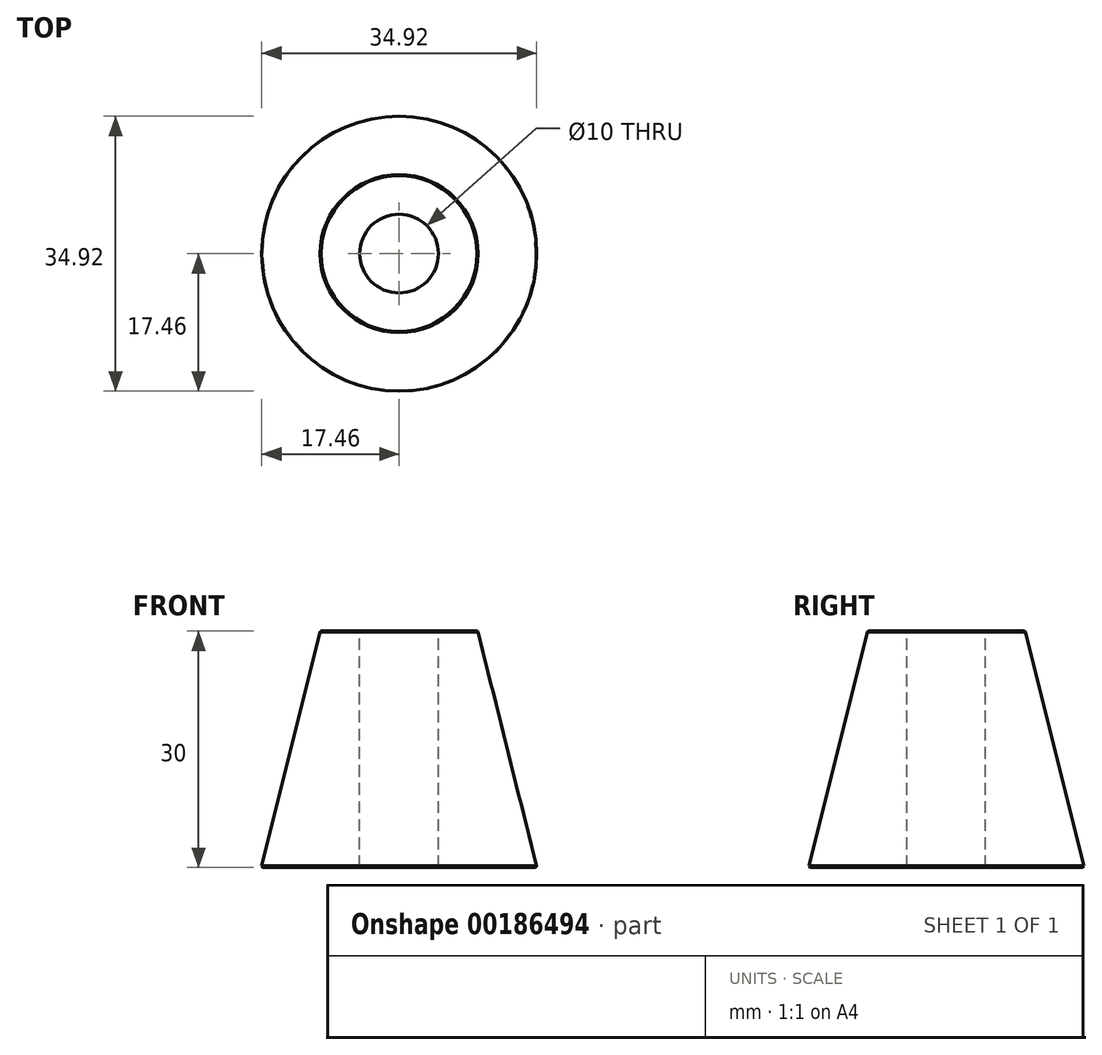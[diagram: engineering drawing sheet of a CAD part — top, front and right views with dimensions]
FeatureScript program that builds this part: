
annotation { "Feature Type Name" : "Feature", "Feature Type Description" : "" }
export const myFeature = defineFeature(function(context is Context, id is Id, definition is map)
    precondition{}
    {
        {
            var Q0;
            Q0=qCreatedBy(makeId("Front.planeOp"),FACE);
            var sketch = newSketch(context, id + "F0", { "sketchPlane" : qUnion([Q0])});
            skLineSegment(sketch, "E0", {"start": v(0, 0) * mm, "end": v(-17.5, 0) * mm});
            skLineSegment(sketch, "E1", {"start": v(-17.5, 0) * mm, "end": v(-10, 30) * mm});
            skLineSegment(sketch, "E2", {"start": v(-10, 30) * mm, "end": v(0, 30) * mm});
            skLineSegment(sketch, "E3", {"start": v(0, 30) * mm, "end": v(0, 0) * mm});
            skLineSegment(sketch, "E4", {"start": v(0, 50.18) * mm, "end": v(0, -26.59) * mm, "construction": true});
            skSolve(sketch);
        }
        {
            var Q0;
            Q0=makeQuery(id+"F0.imprint","IMPRINT",FACE,{"disambiguationData":[TD([[makeQuery(id+"F0.imprint","IMPRINT",EDGE,{"derivedFrom":sQuery(id+"F0.wireOp",EDGE,"E0")}),-1.0]])]});
            var Q1;
            Q1=sQuery(id+"F0.wireOp",EDGE,"E4");
            revolve(context, id + "F1", {"entities" : qUnion([Q0]), "axis" : qUnion([Q1]), "revolveType" : RevolveType.FULL});
        }
        {
            var Q0;
            Q0=makeQuery(id+"F1.opRevolve","SWEPT_EDGE",EDGE,{"disambiguationData":[OSD([sQuery(id+"F0.wireOp",EDGE,"E1"),sQuery(id+"F0.wireOp",EDGE,"E2")])]});
            var Q1;
            Q1=makeQuery(id+"F1.opRevolve","SWEPT_EDGE",EDGE,{"disambiguationData":[OSD([sQuery(id+"F0.wireOp",EDGE,"E0"),sQuery(id+"F0.wireOp",EDGE,"E1")])]});
            chamfer(context, id + "F2", {"entities" : qUnion([Q0, Q1]), "width" : 0.13 * mm, "tangentPropagation" : true});
        }
        {
            var Q0;
            Q0=makeQuery(id+"F1.opRevolve","SWEPT_FACE",FACE,{"disambiguationData":[OSD([sQuery(id+"F0.wireOp",EDGE,"E2")])]});
            var sketch = newSketch(context, id + "F3", { "sketchPlane" : qUnion([Q0])});
            skCircle(sketch, "E5", {"center": v(0, 0) * mm, "radius": 5 * mm});
            skSolve(sketch);
        }
        {
            var Q0;
            Q0 = qSketchRegion(id + "F3", true);
            extrude(context, id + "F4", {"entities" : qUnion([Q0]), "operationType" : NewBodyOperationType.REMOVE, "endBound" : BoundingType.UP_TO_NEXT, "oppositeDirection" : true, "depth" : 25.4 * mm});
        }
    });
